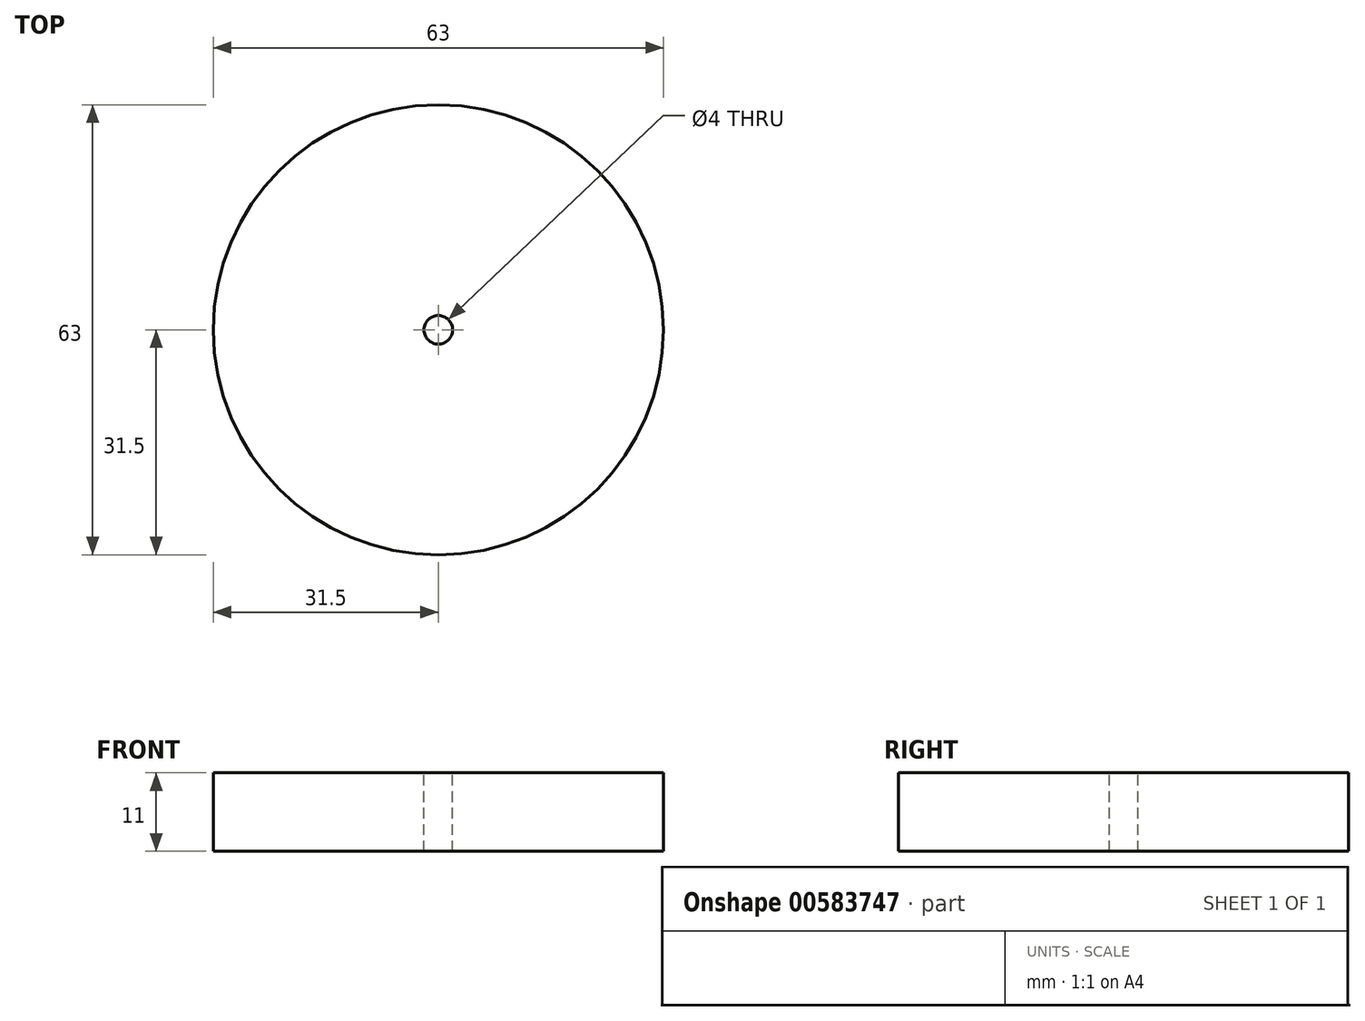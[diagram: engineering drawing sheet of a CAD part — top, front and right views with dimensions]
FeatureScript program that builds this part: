
annotation { "Feature Type Name" : "Feature", "Feature Type Description" : "" }
export const myFeature = defineFeature(function(context is Context, id is Id, definition is map)
    precondition{}
    {
        {
            var Q0;
            Q0=qCreatedBy(makeId("Top.planeOp"),FACE);
            var sketch = newSketch(context, id + "F0", { "sketchPlane" : qUnion([Q0])});
            skCircle(sketch, "E0", {"center": v(0, 0) * mm, "radius": 31.5 * mm});
            skSolve(sketch);
        }
        {
            var Q0;
            Q0 = qSketchRegion(id + "F0", true);
            var Q1;
            Q1=makeQuery(id+"F0.imprint","IMPRINT",FACE,{"disambiguationData":[TD([[makeQuery(id+"F0.imprint","IMPRINT",EDGE,{"derivedFrom":sQuery(id+"F0.wireOp",EDGE,"E0")}),1.0]])]});
            extrude(context, id + "F1", {"entities" : qUnion([Q0, Q1]), "depth" : 11 * mm, "offsetDistance" : 25 * mm});
        }
        {
            var Q0;
            Q0=makeQuery(id+"F1.opExtrude","CAP_FACE",FACE,{"disambiguationData":[OSD([sQuery(id+"F0.wireOp",EDGE,"E0")])],"isStart":false});
            var sketch = newSketch(context, id + "F2", { "sketchPlane" : qUnion([Q0])});
            skPoint(sketch, "E1", {"position": v(0, 0) * mm});
            skSolve(sketch);
        }
        {
            var Q0;
            Q0=sQuery(id+"F2.wireOp",VERTEX,"E1");
            var Q1;
            Q1=makeQuery(id+"F1.opExtrude","SWEPT_BODY",BODY,{"disambiguationData":[OSD([sQuery(id+"F0.wireOp",EDGE,"E0")])]});
            hole(context, id + "F3", {"style" : HoleStyle.SIMPLE, "endStyle" : HoleEndStyle.THROUGH, "holeDiameter" : 4 * mm, "majorDiameter" : 5 * mm, "isTappedThrough" : true, "tappedDepth" : 12 * mm, "tapClearance" : 3, "locations" : qUnion([Q0]), "scope" : qUnion([Q1])});
        }
    });
